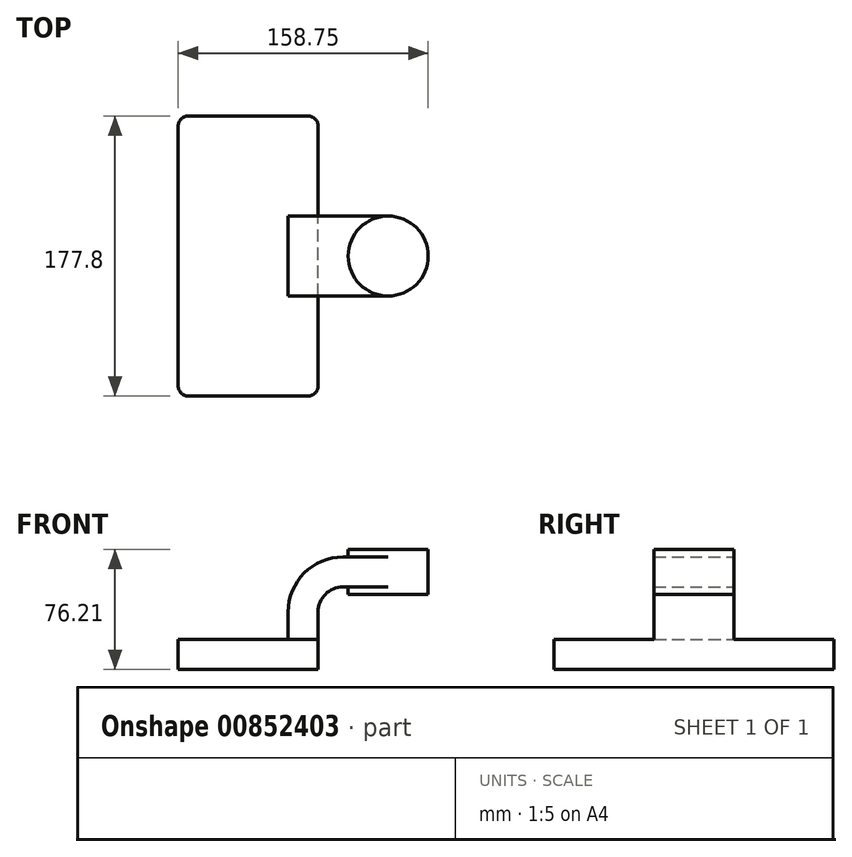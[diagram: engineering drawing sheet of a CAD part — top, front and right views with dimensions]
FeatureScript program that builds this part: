
annotation { "Feature Type Name" : "Feature", "Feature Type Description" : "" }
export const myFeature = defineFeature(function(context is Context, id is Id, definition is map)
    precondition{}
    {
        {
            var Q0;
            Q0=qCreatedBy(makeId("Front.planeOp"),FACE);
            var sketch = newSketch(context, id + "F0", { "sketchPlane" : qUnion([Q0])});
            skLineSegment(sketch, "E0.bottom", {"start": v(44.45, 9.53) * mm, "end": v(-44.45, 9.53) * mm});
            skLineSegment(sketch, "E0.top", {"start": v(44.45, -9.53) * mm, "end": v(-44.45, -9.53) * mm});
            skLineSegment(sketch, "E0.left", {"start": v(44.45, 9.53) * mm, "end": v(44.45, -9.53) * mm});
            skLineSegment(sketch, "E0.right", {"start": v(-44.45, 9.53) * mm, "end": v(-44.45, -9.53) * mm});
            skPoint(sketch, "E0.middle", {"position": v(0, 0) * mm});
            skLineSegment(sketch, "E1.bottom", {"start": v(63.5, 66.67) * mm, "end": v(114.3, 66.67) * mm});
            skLineSegment(sketch, "E1.top", {"start": v(63.5, 38.1) * mm, "end": v(114.3, 38.1) * mm});
            skLineSegment(sketch, "E1.left", {"start": v(63.5, 66.67) * mm, "end": v(63.5, 38.1) * mm});
            skLineSegment(sketch, "E1.right", {"start": v(114.3, 66.67) * mm, "end": v(114.3, 38.1) * mm});
            skLineSegment(sketch, "E2", {"start": v(88.9, 66.67) * mm, "end": v(88.9, 38.1) * mm});
            skLineSegment(sketch, "E3", {"start": v(44.45, 9.53) * mm, "end": v(44.45, 27) * mm});
            skLineSegment(sketch, "E4", {"start": v(88.9, 42.88) * mm, "end": v(60.32, 42.88) * mm});
            skArc(sketch, "E5", {"start": v(44.45, 27) * mm, "mid": v(49.1, 38.23) * mm, "end": v(60.32, 42.88) * mm});
            skLineSegment(sketch, "E6.0", {"start": v(88.9, 61.93) * mm, "end": v(60.32, 61.93) * mm});
            skArc(sketch, "E6.1", {"start": v(25.4, 27) * mm, "mid": v(35.63, 51.7) * mm, "end": v(60.32, 61.93) * mm});
            skLineSegment(sketch, "E6.2", {"start": v(25.4, 9.53) * mm, "end": v(25.4, 27) * mm});
            skFitSpline(sketch, "E7", {"points": [v(60.32, 61.93) * mm, v(-44.45, 9.53) * mm], "startDerivative": vector(-118.27, 0) * mm, "endDerivative": vector(0, -71.82) * mm});
            skSolve(sketch);
        }
        {
            var Q0;
            Q0=makeQuery(id+"F0.imprint","IMPRINT",FACE,{"disambiguationData":[TD([[makeQuery(id+"F0.imprint","IMPRINT",EDGE,{"derivedFrom":sQuery(id+"F0.wireOp",EDGE,"E0.bottom")}),1.0]])]});
            extrude(context, id + "F1", {"entities" : qUnion([Q0]), "endBound" : BoundingType.SYMMETRIC, "depth" : 177.8 * mm, "offsetDistance" : 25.4 * mm});
        }
        {
            var Q0;
            {var subQ4=sQuery(id+"F0.wireOp",EDGE,"E3");Q0=makeQuery(id+"F0.imprint","IMPRINT",FACE,{"disambiguationData":[TD([[makeQuery(id+"F0.imprint","IMPRINT",EDGE,{"derivedFrom":subQ4}),1.0]])]});}
            var Q1;
            {var subQ0=sQuery(id+"F0.wireOp",EDGE,"E6.0");var subQ1=sQuery(id+"F0.wireOp",EDGE,"E1.left");var subQ2=makeQuery(id+"F0.imprint","INTERSECT",VERTEX,{"derivedFrom":[subQ1,subQ0]});Q1=makeQuery(id+"F0.imprint","IMPRINT",FACE,{"disambiguationData":[TD([[makeQuery(id+"F0.imprint","IMPRINT",EDGE,{"disambiguationData":[TD([[subQ2,-1.0]])],"derivedFrom":subQ1}),1.0]])]});}
            extrude(context, id + "F2", {"entities" : qUnion([Q0, Q1]), "operationType" : NewBodyOperationType.ADD, "endBound" : BoundingType.SYMMETRIC, "depth" : 50.8 * mm, "offsetDistance" : 25.4 * mm});
        }
        {
            var Q0;
            Q0=makeQuery(id+"F0.imprint","IMPRINT",FACE,{"disambiguationData":[TD([[makeQuery(id+"F0.imprint","IMPRINT",EDGE,{"derivedFrom":sQuery(id+"F0.wireOp",EDGE,"E6.1")}),1.0]])]});
            extrude(context, id + "F3", {"entities" : qUnion([Q0]), "operationType" : NewBodyOperationType.ADD, "endBound" : BoundingType.SYMMETRIC, "depth" : 15.88 * mm, "offsetDistance" : 25.4 * mm});
        }
        {
            var Q0;
            {var subQ0=sQuery(id+"F0.wireOp",EDGE,"E1.right");Q0=makeQuery(id+"F0.imprint","IMPRINT",FACE,{"disambiguationData":[TD([[makeQuery(id+"F0.imprint","IMPRINT",EDGE,{"derivedFrom":subQ0}),-1.0]])]});}
            var Q1;
            Q1=sQuery(id+"F0.wireOp",EDGE,"E2");
            revolve(context, id + "F4", {"operationType" : NewBodyOperationType.ADD, "surfaceOperationType" : NewSurfaceOperationType.NEW, "entities" : qUnion([Q0]), "axis" : qUnion([Q1]), "revolveType" : RevolveType.FULL});
        }
        {
            var Q0;
            Q0=makeQuery(id+"F1.opExtrude","CAP_EDGE",EDGE,{"disambiguationData":[OSD([sQuery(id+"F0.wireOp",EDGE,"E0.left")])],"isStart":false});
            var Q1;
            Q1=makeQuery(id+"F1.opExtrude","CAP_EDGE",EDGE,{"disambiguationData":[OSD([sQuery(id+"F0.wireOp",EDGE,"E0.right")])],"isStart":false});
            var Q2;
            Q2=makeQuery(id+"F1.opExtrude","CAP_EDGE",EDGE,{"disambiguationData":[OSD([sQuery(id+"F0.wireOp",EDGE,"E0.right")])],"isStart":true});
            var Q3;
            Q3=makeQuery(id+"F1.opExtrude","CAP_EDGE",EDGE,{"disambiguationData":[OSD([sQuery(id+"F0.wireOp",EDGE,"E0.left")])],"isStart":true});
            fillet(context, id + "F5", {"entities" : qUnion([Q0, Q1, Q2, Q3]), "radius" : 6.35 * mm, "tangentPropagation" : true, "allowEdgeOverflow" : false});
        }
    });
